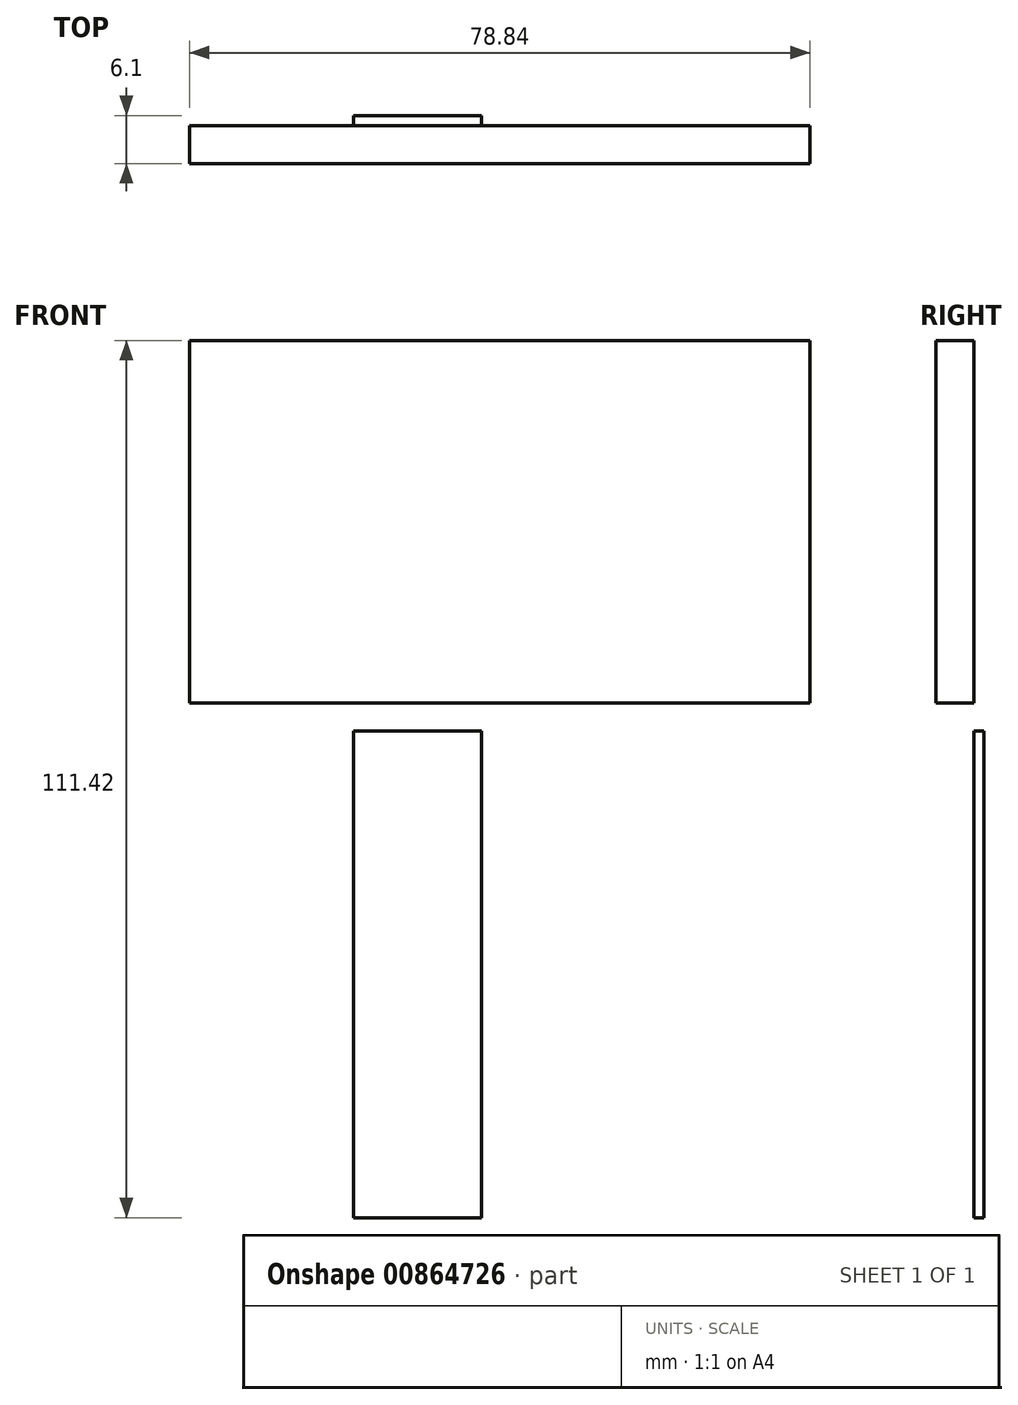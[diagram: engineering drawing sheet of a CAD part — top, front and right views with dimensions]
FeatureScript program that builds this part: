
annotation { "Feature Type Name" : "Feature", "Feature Type Description" : "" }
export const myFeature = defineFeature(function(context is Context, id is Id, definition is map)
    precondition{}
    {
        {
            var Q0;
            Q0=qCreatedBy(makeId("Front.planeOp"),FACE);
            var sketch = newSketch(context, id + "F0", { "sketchPlane" : qUnion([Q0])});
            skLineSegment(sketch, "E0.bottom", {"start": v(-93.3, 55.4) * mm, "end": v(-14.45, 55.4) * mm});
            skLineSegment(sketch, "E0.top", {"start": v(-93.3, 9.36) * mm, "end": v(-14.45, 9.36) * mm});
            skLineSegment(sketch, "E0.left", {"start": v(-93.3, 55.4) * mm, "end": v(-93.3, 9.36) * mm});
            skLineSegment(sketch, "E0.right", {"start": v(-14.45, 55.4) * mm, "end": v(-14.45, 9.36) * mm});
            skSolve(sketch);
        }
        {
            var Q0;
            Q0=makeQuery(id+"F0.imprint","IMPRINT",FACE,{"disambiguationData":[TD([[makeQuery(id+"F0.imprint","IMPRINT",EDGE,{"derivedFrom":sQuery(id+"F0.wireOp",EDGE,"E0.bottom")}),-1.0]])]});
            extrude(context, id + "F1", {"entities" : qUnion([Q0]), "depth" : 3.05 * mm, "offsetDistance" : 25.4 * mm});
        }
        {
            var Q0;
            Q0=makeQuery(id+"F1.opExtrude","CAP_FACE",FACE,{"disambiguationData":[OSD([sQuery(id+"F0.wireOp",EDGE,"E0.bottom"),sQuery(id+"F0.wireOp",EDGE,"E0.top"),sQuery(id+"F0.wireOp",EDGE,"E0.left"),sQuery(id+"F0.wireOp",EDGE,"E0.right")])],"isStart":false});
            extrude(context, id + "F2", {"entities" : qUnion([Q0]), "operationType" : NewBodyOperationType.ADD, "depth" : 1.78 * mm, "offsetDistance" : 25.4 * mm});
        }
        {
            var Q0;
            Q0=qCreatedBy(makeId("Front.planeOp"),FACE);
            var sketch = newSketch(context, id + "F3", { "sketchPlane" : qUnion([Q0])});
            skLineSegment(sketch, "E1.bottom", {"start": v(-72.42, 5.76) * mm, "end": v(-56.2, 5.76) * mm});
            skLineSegment(sketch, "E1.top", {"start": v(-72.42, -56.03) * mm, "end": v(-56.2, -56.03) * mm});
            skLineSegment(sketch, "E1.left", {"start": v(-72.42, 5.76) * mm, "end": v(-72.42, -56.03) * mm});
            skLineSegment(sketch, "E1.right", {"start": v(-56.2, 5.76) * mm, "end": v(-56.2, -56.03) * mm});
            skSolve(sketch);
        }
        {
            var Q0;
            Q0=makeQuery(id+"F3.imprint","IMPRINT",FACE,{"disambiguationData":[TD([[makeQuery(id+"F3.imprint","IMPRINT",EDGE,{"derivedFrom":sQuery(id+"F3.wireOp",EDGE,"E1.bottom")}),-1.0]])]});
            extrude(context, id + "F4", {"entities" : qUnion([Q0]), "oppositeDirection" : true, "depth" : 1.27 * mm, "offsetDistance" : 25.4 * mm});
        }
    });
